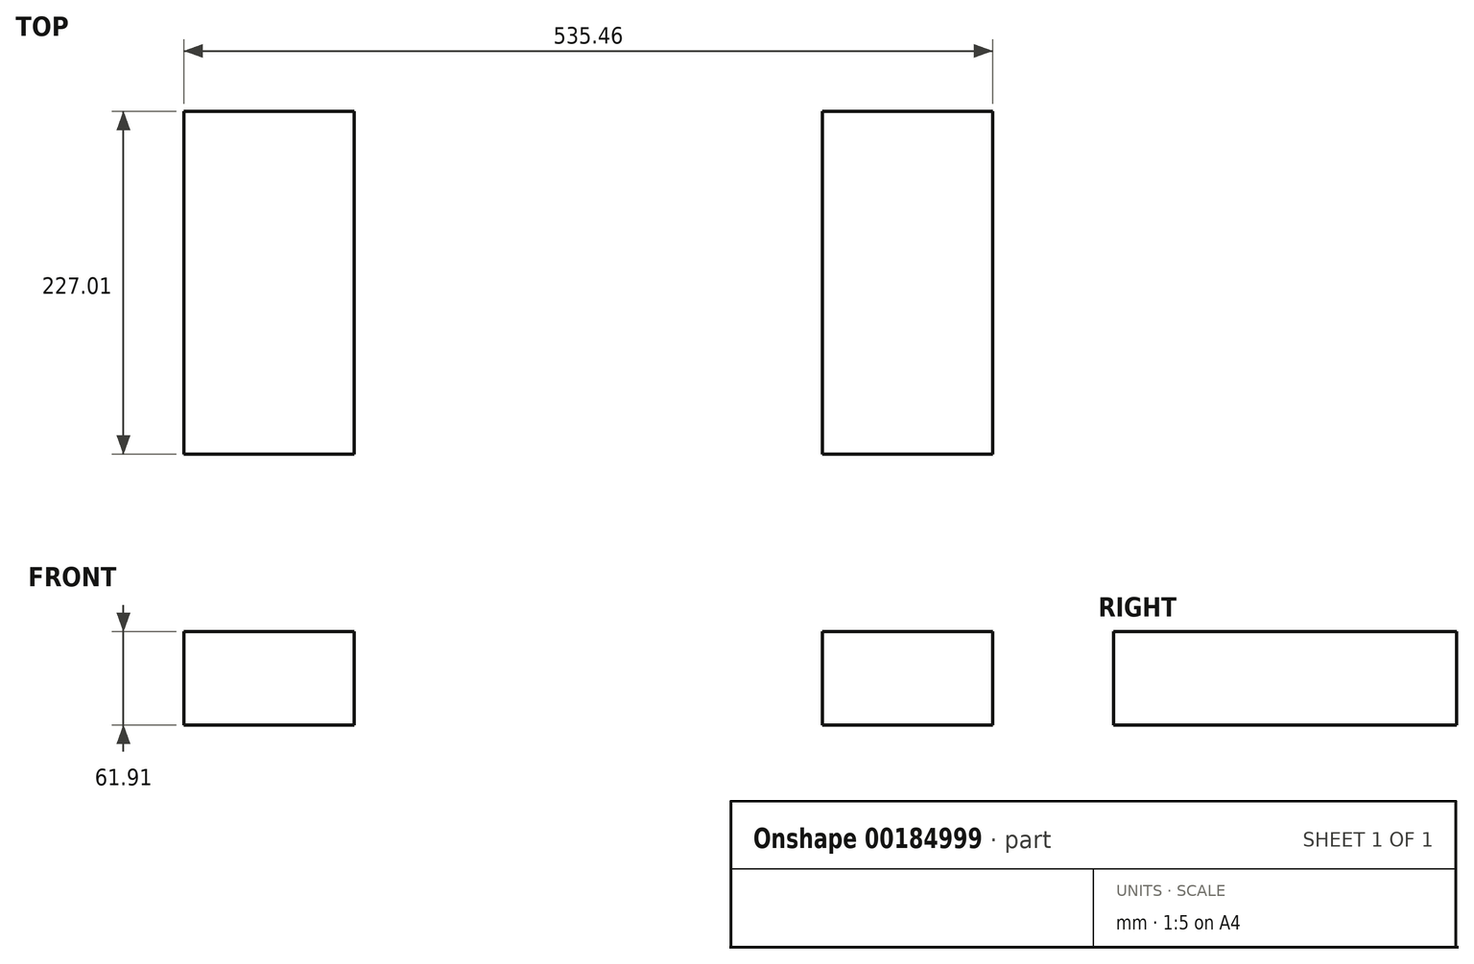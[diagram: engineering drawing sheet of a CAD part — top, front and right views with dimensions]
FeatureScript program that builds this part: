
annotation { "Feature Type Name" : "Feature", "Feature Type Description" : "" }
export const myFeature = defineFeature(function(context is Context, id is Id, definition is map)
    precondition{}
    {
        {
            var Q0;
            Q0=qCreatedBy(makeId("Front.planeOp"),FACE);
            var sketch = newSketch(context, id + "F0", { "sketchPlane" : qUnion([Q0])});
            skLineSegment(sketch, "E0.bottom", {"start": v(155.02, 61.91) * mm, "end": v(267.73, 61.91) * mm});
            skLineSegment(sketch, "E0.top", {"start": v(155.02, 0) * mm, "end": v(267.73, 0) * mm});
            skLineSegment(sketch, "E0.left", {"start": v(155.02, 61.91) * mm, "end": v(155.02, 0) * mm});
            skLineSegment(sketch, "E0.right", {"start": v(267.73, 61.91) * mm, "end": v(267.73, 0) * mm});
            skLineSegment(sketch, "E1.MirrorCS", {"start": v(-155.02, 61.91) * mm, "end": v(-155.02, 0) * mm});
            skLineSegment(sketch, "E2.MirrorCS", {"start": v(-155.02, 61.91) * mm, "end": v(-267.73, 61.91) * mm});
            skLineSegment(sketch, "E3.MirrorCS", {"start": v(-267.73, 61.91) * mm, "end": v(-267.73, 0) * mm});
            skLineSegment(sketch, "E4.MirrorCS", {"start": v(-155.02, 0) * mm, "end": v(-267.73, 0) * mm});
            skSolve(sketch);
        }
        {
            var Q0;
            Q0=makeQuery(id+"F0.imprint","IMPRINT",FACE,{"disambiguationData":[TD([[makeQuery(id+"F0.imprint","IMPRINT",EDGE,{"derivedFrom":sQuery(id+"F0.wireOp",EDGE,"E0.bottom")}),-1.0]])]});
            var Q1;
            Q1=makeQuery(id+"F0.imprint","IMPRINT",FACE,{"disambiguationData":[TD([[makeQuery(id+"F0.imprint","IMPRINT",EDGE,{"derivedFrom":sQuery(id+"F0.wireOp",EDGE,"E1.MirrorCS")}),-1.0]])]});
            extrude(context, id + "F1", {"entities" : qUnion([Q0, Q1]), "oppositeDirection" : true, "depth" : 227 * mm});
        }
    });
